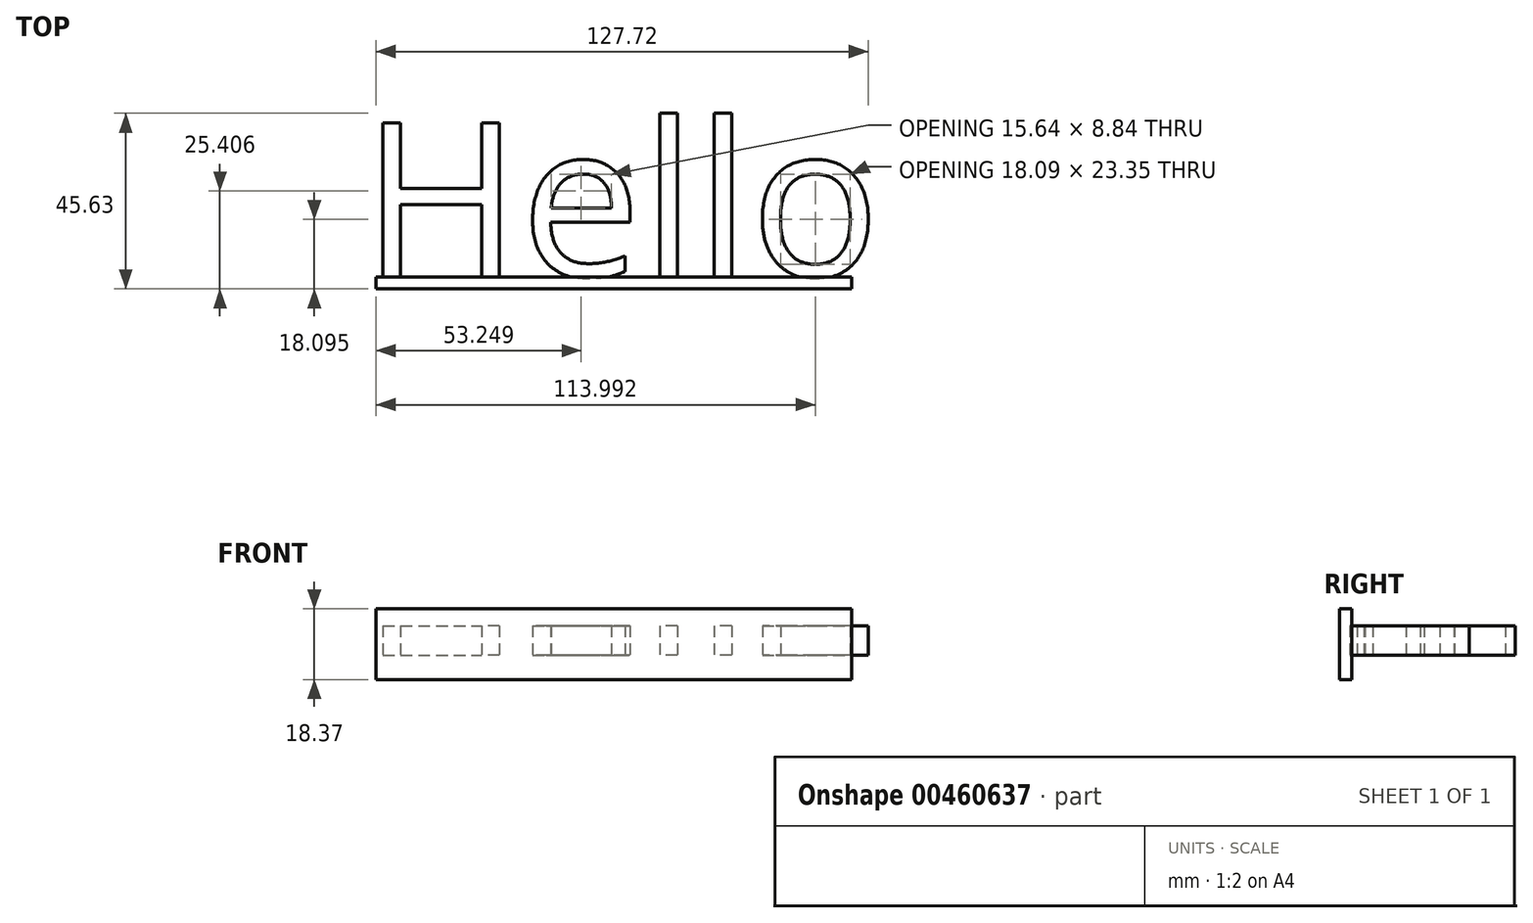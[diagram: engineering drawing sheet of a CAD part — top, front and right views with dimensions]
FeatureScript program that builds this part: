
annotation { "Feature Type Name" : "Feature", "Feature Type Description" : "" }
export const myFeature = defineFeature(function(context is Context, id is Id, definition is map)
    precondition{}
    {
        {
            var Q0;
            Q0=qCreatedBy(makeId("Top.planeOp"),FACE);
            var sketch = newSketch(context, id + "F0", { "sketchPlane" : qUnion([Q0])});
            skText(sketch, "E0", { "text": "Hello\n", "fontName": "OpenSans-Regular.ttf"});
            const initialGuessF0  = {"E0": [-0.06545, -0.02066, 1, 0, 0.04023]};
            skSetInitialGuess(sketch, initialGuessF0);
            skSolve(sketch);
        }
        {
            var Q0;
            Q0 = qSketchRegion(id + "F0", true);
            extrude(context, id + "F1", {"entities" : qUnion([Q0]), "depth" : 7.62 * mm});
        }
        {
            var Q0;
            Q0=qCreatedBy(makeId("Right.planeOp"),FACE);
            var sketch = newSketch(context, id + "F2", { "sketchPlane" : qUnion([Q0])});
            skLineSegment(sketch, "E1.right", {"start": v(63.99, -23.58) * mm, "end": v(63.99, -21.03) * mm});
            skLineSegment(sketch, "E2.bottom", {"start": v(-23.83, -6.36) * mm, "end": v(-20.66, -6.36) * mm});
            skLineSegment(sketch, "E2.top", {"start": v(-23.83, 12.01) * mm, "end": v(-20.66, 12.01) * mm});
            skLineSegment(sketch, "E2.left", {"start": v(-23.83, -6.36) * mm, "end": v(-23.83, 12.01) * mm});
            skLineSegment(sketch, "E2.right", {"start": v(-20.66, -6.36) * mm, "end": v(-20.66, 12.01) * mm});
            skSolve(sketch);
        }
        {
            var Q0;
            Q0=makeQuery(id+"F2.imprint","IMPRINT",FACE,{"disambiguationData":[TD([[makeQuery(id+"F2.imprint","IMPRINT",EDGE,{"derivedFrom":sQuery(id+"F2.wireOp",EDGE,"E2.bottom")}),1.0]])]});
            extrude(context, id + "F3", {"entities" : qUnion([Q0]), "endBound" : BoundingType.SYMMETRIC, "depth" : 123.44 * mm});
        }
    });
